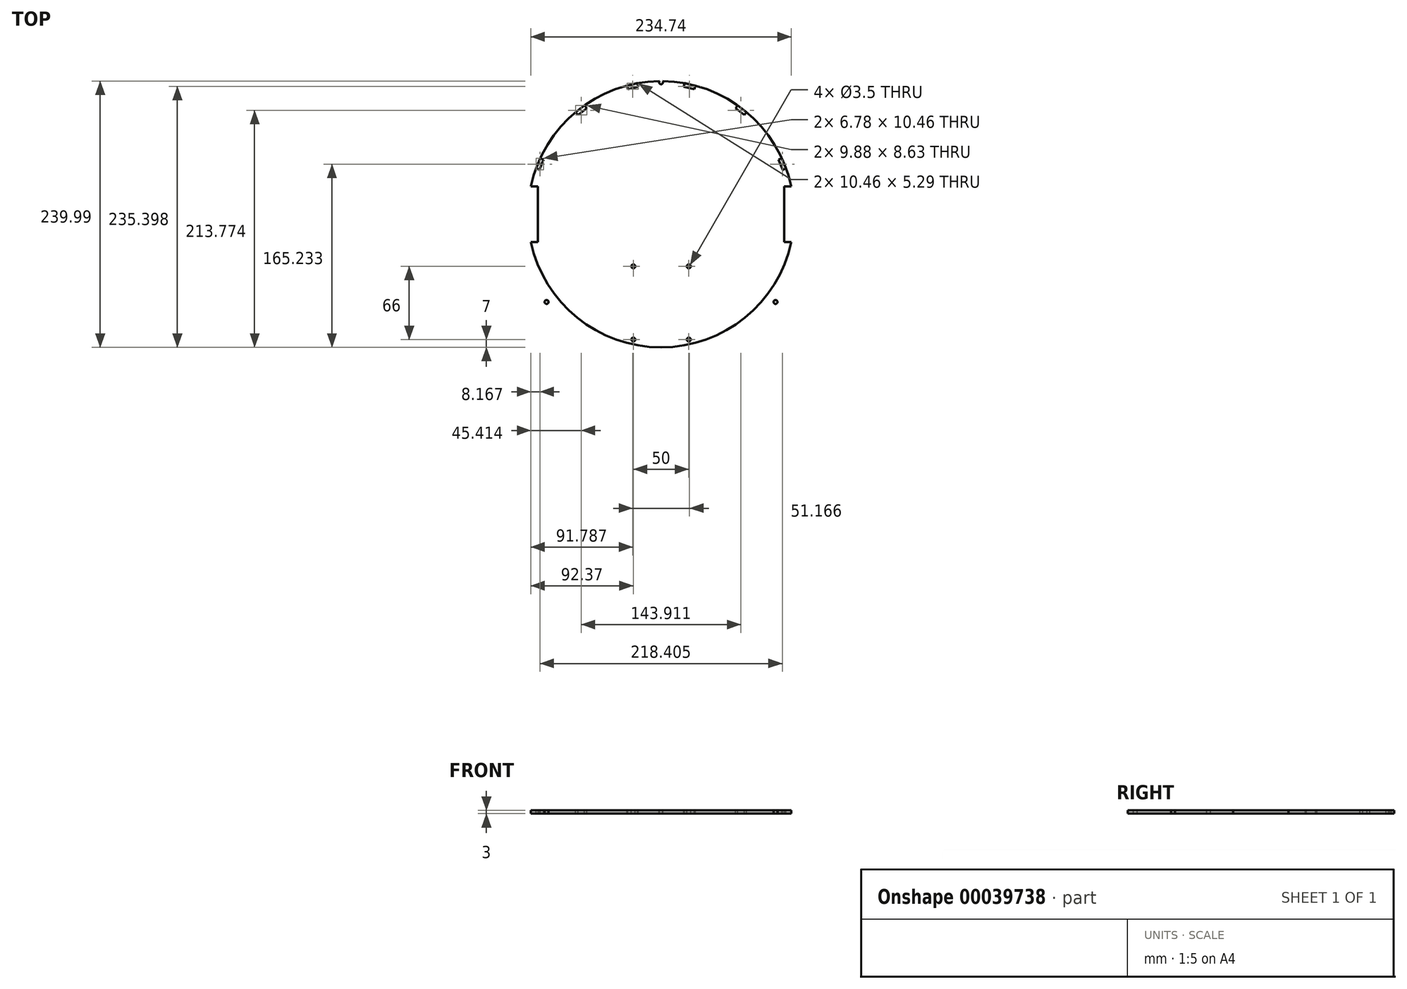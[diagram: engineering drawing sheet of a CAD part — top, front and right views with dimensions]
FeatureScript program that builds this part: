
annotation { "Feature Type Name" : "Feature", "Feature Type Description" : "" }
export const myFeature = defineFeature(function(context is Context, id is Id, definition is map)
    precondition{}
    {
        {
            var Q0;
            Q0=qCreatedBy(makeId("Top.planeOp"),FACE);
            var sketch = newSketch(context, id + "F0", { "sketchPlane" : qUnion([Q0])});
            skCircle(sketch, "E0", {"center": v(0, 0) * mm, "radius": 150 * mm});
            skLineSegment(sketch, "E1.bottom", {"start": v(-125, 25) * mm, "end": v(-111, 25) * mm});
            skLineSegment(sketch, "E1.top", {"start": v(-125, -25) * mm, "end": v(-111, -25) * mm});
            skLineSegment(sketch, "E1.left", {"start": v(-125, 25) * mm, "end": v(-125, -25) * mm});
            skLineSegment(sketch, "E1.right", {"start": v(-111, 25) * mm, "end": v(-111, -25) * mm});
            skLineSegment(sketch, "E2.bottom", {"start": v(125, 25) * mm, "end": v(111, 25) * mm});
            skLineSegment(sketch, "E2.top", {"start": v(125, -25) * mm, "end": v(111, -25) * mm});
            skLineSegment(sketch, "E2.left", {"start": v(125, 25) * mm, "end": v(125, -25) * mm});
            skLineSegment(sketch, "E2.right", {"start": v(111, 25) * mm, "end": v(111, -25) * mm});
            skCircle(sketch, "E3", {"center": v(-138, 19) * mm, "radius": 1.75 * mm});
            skCircle(sketch, "E4", {"center": v(-138, -19) * mm, "radius": 1.75 * mm});
            skCircle(sketch, "E5", {"center": v(138, 19) * mm, "radius": 1.75 * mm});
            skCircle(sketch, "E6", {"center": v(138, -19) * mm, "radius": 1.75 * mm});
            skSolve(sketch);
        }
        {
            var Q0;
            Q0=makeQuery(id+"F0.imprint","IMPRINT",FACE,{"disambiguationData":[TD([[makeQuery(id+"F0.imprint","IMPRINT",EDGE,{"derivedFrom":sQuery(id+"F0.wireOp",EDGE,"E0")}),1.0]])]});
            extrude(context, id + "F1", {"entities" : qUnion([Q0]), "depth" : 3 * mm});
        }
        {
            var Q0;
            Q0=makeQuery(id+"F1.opExtrude","CAP_FACE",FACE,{"disambiguationData":[OSD([sQuery(id+"F0.wireOp",EDGE,"E0"),sQuery(id+"F0.wireOp",EDGE,"E1.bottom"),sQuery(id+"F0.wireOp",EDGE,"E1.top"),sQuery(id+"F0.wireOp",EDGE,"E1.left"),sQuery(id+"F0.wireOp",EDGE,"E1.right"),sQuery(id+"F0.wireOp",EDGE,"E2.bottom"),sQuery(id+"F0.wireOp",EDGE,"E2.top"),sQuery(id+"F0.wireOp",EDGE,"E2.left"),sQuery(id+"F0.wireOp",EDGE,"E2.right")])],"isStart":false});
            var sketch = newSketch(context, id + "F2", { "sketchPlane" : qUnion([Q0])});
            skCircle(sketch, "E7", {"center": v(0, 0) * mm, "radius": 130 * mm, "construction": true});
            skLineSegment(sketch, "E8", {"start": v(0, 0) * mm, "end": v(0, 150) * mm, "construction": true});
            skLineSegment(sketch, "E9", {"start": v(0, 0) * mm, "end": v(-63.4, 135.95) * mm, "construction": true});
            skLineSegment(sketch, "E10", {"start": v(0, 0) * mm, "end": v(63.4, 135.95) * mm, "construction": true});
            skLineSegment(sketch, "E11", {"start": v(0, 0) * mm, "end": v(-147.72, 26.05) * mm, "construction": true});
            skLineSegment(sketch, "E12", {"start": v(0, 0) * mm, "end": v(147.72, 26.05) * mm, "construction": true});
            skCircle(sketch, "E13", {"center": v(-123.26, 41.31) * mm, "radius": 1.75 * mm});
            skCircle(sketch, "E14", {"center": v(-116.37, 57.94) * mm, "radius": 1.75 * mm});
            skCircle(sketch, "E15", {"center": v(-86.09, 97.4) * mm, "radius": 1.75 * mm});
            skCircle(sketch, "E16", {"center": v(-71.8, 108.37) * mm, "radius": 1.75 * mm});
            skCircle(sketch, "E17", {"center": v(-36.86, 124.67) * mm, "radius": 1.75 * mm});
            skCircle(sketch, "E18", {"center": v(-19.28, 128.56) * mm, "radius": 1.75 * mm});
            skCircle(sketch, "E19", {"center": v(19.28, 128.56) * mm, "radius": 1.75 * mm});
            skCircle(sketch, "E20", {"center": v(36.86, 124.67) * mm, "radius": 1.75 * mm});
            skCircle(sketch, "E21", {"center": v(71.8, 108.37) * mm, "radius": 1.75 * mm});
            skCircle(sketch, "E22", {"center": v(86.09, 97.4) * mm, "radius": 1.75 * mm});
            skCircle(sketch, "E23", {"center": v(116.37, 57.94) * mm, "radius": 1.75 * mm});
            skCircle(sketch, "E24", {"center": v(123.26, 41.31) * mm, "radius": 1.75 * mm});
            skLineSegment(sketch, "E25", {"start": v(0, 0) * mm, "end": v(-138.58, 57.4) * mm, "construction": true});
            skLineSegment(sketch, "E26", {"start": v(0, 0) * mm, "end": v(-91.31, 119) * mm, "construction": true});
            skLineSegment(sketch, "E27", {"start": v(0, 0) * mm, "end": v(-32.47, 146.44) * mm, "construction": true});
            skLineSegment(sketch, "E28", {"start": v(0, 0) * mm, "end": v(32.47, 146.44) * mm, "construction": true});
            skLineSegment(sketch, "E29", {"start": v(0, 0) * mm, "end": v(91.31, 119) * mm, "construction": true});
            skLineSegment(sketch, "E30", {"start": v(0, 0) * mm, "end": v(138.58, 57.4) * mm, "construction": true});
            skLineSegment(sketch, "E31", {"start": v(-130.33, 48.57) * mm, "end": v(-126.5, 57.81) * mm});
            skLineSegment(sketch, "E32", {"start": v(-126.5, 57.81) * mm, "end": v(-123.55, 56.59) * mm});
            skLineSegment(sketch, "E33", {"start": v(-123.55, 56.59) * mm, "end": v(-127.38, 47.35) * mm});
            skLineSegment(sketch, "E34", {"start": v(-127.38, 47.35) * mm, "end": v(-130.33, 48.57) * mm});
            skPoint(sketch, "E35", {"position": v(-128.42, 53.2) * mm});
            skLineSegment(sketch, "E36", {"start": v(-108.77, 50.46) * mm, "end": v(-112.6, 41.23) * mm});
            skLineSegment(sketch, "E37", {"start": v(-112.6, 41.23) * mm, "end": v(-109.64, 40) * mm});
            skLineSegment(sketch, "E38", {"start": v(-109.64, 40) * mm, "end": v(-105.81, 49.24) * mm});
            skLineSegment(sketch, "E39", {"start": v(-105.81, 49.24) * mm, "end": v(-108.77, 50.46) * mm});
            skPoint(sketch, "E40", {"position": v(-110.68, 45.85) * mm});
            skCircle(sketch, "E41", {"center": v(-118.07, 48.9) * mm, "radius": 1.75 * mm});
            skLineSegment(sketch, "E42.1.0", {"start": v(-78.7, 110.78) * mm, "end": v(-86.64, 104.7) * mm});
            skLineSegment(sketch, "E42.1.1", {"start": v(-88.58, 107.23) * mm, "end": v(-80.65, 113.32) * mm});
            skPoint(sketch, "E42.1.2", {"position": v(-84.62, 110.28) * mm});
            skLineSegment(sketch, "E42.1.3", {"start": v(-80.65, 113.32) * mm, "end": v(-78.7, 110.78) * mm});
            skLineSegment(sketch, "E42.1.4", {"start": v(-86.64, 104.7) * mm, "end": v(-88.58, 107.23) * mm});
            skPoint(sketch, "E42.1.5", {"position": v(-84.62, 110.28) * mm});
            skCircle(sketch, "E42.1.6", {"center": v(-77.8, 101.4) * mm, "radius": 1.75 * mm});
            skLineSegment(sketch, "E42.1.7", {"start": v(-68.96, 98.09) * mm, "end": v(-76.9, 92) * mm});
            skLineSegment(sketch, "E42.1.8", {"start": v(-74.95, 89.46) * mm, "end": v(-67.01, 95.55) * mm});
            skLineSegment(sketch, "E42.1.9", {"start": v(-67.01, 95.55) * mm, "end": v(-68.96, 98.09) * mm});
            skPoint(sketch, "E42.1.10", {"position": v(-72.93, 95.04) * mm});
            skLineSegment(sketch, "E42.1.11", {"start": v(-76.9, 92) * mm, "end": v(-74.95, 89.46) * mm});
            skLineSegment(sketch, "E42.anchor1", {"start": v(0, 0) * mm, "end": v(-118.07, 48.9) * mm, "construction": true});
            skLineSegment(sketch, "E42.anchor2", {"start": v(0, 0) * mm, "end": v(-77.8, 101.4) * mm, "construction": true});
            skLineSegment(sketch, "E43.1.0", {"start": v(78.7, 110.78) * mm, "end": v(80.65, 113.32) * mm});
            skLineSegment(sketch, "E43.1.1", {"start": v(86.64, 104.7) * mm, "end": v(78.7, 110.78) * mm});
            skLineSegment(sketch, "E43.1.2", {"start": v(88.58, 107.23) * mm, "end": v(86.64, 104.7) * mm});
            skCircle(sketch, "E43.1.3", {"center": v(77.8, 101.4) * mm, "radius": 1.75 * mm});
            skLineSegment(sketch, "E43.1.4", {"start": v(80.65, 113.32) * mm, "end": v(88.58, 107.23) * mm});
            skPoint(sketch, "E43.1.5", {"position": v(84.62, 110.28) * mm});
            skPoint(sketch, "E43.1.6", {"position": v(84.62, 110.28) * mm});
            skLineSegment(sketch, "E43.1.7", {"start": v(74.95, 89.46) * mm, "end": v(76.9, 92) * mm});
            skLineSegment(sketch, "E43.1.8", {"start": v(67.01, 95.55) * mm, "end": v(74.95, 89.46) * mm});
            skPoint(sketch, "E43.1.9", {"position": v(72.93, 95.04) * mm});
            skLineSegment(sketch, "E43.1.10", {"start": v(68.96, 98.09) * mm, "end": v(67.01, 95.55) * mm});
            skLineSegment(sketch, "E43.1.11", {"start": v(76.9, 92) * mm, "end": v(68.96, 98.09) * mm});
            skLineSegment(sketch, "E43.1.12", {"start": v(127.38, 47.35) * mm, "end": v(123.55, 56.59) * mm});
            skLineSegment(sketch, "E43.1.13", {"start": v(126.5, 57.81) * mm, "end": v(130.33, 48.57) * mm});
            skLineSegment(sketch, "E43.1.14", {"start": v(123.55, 56.59) * mm, "end": v(126.5, 57.81) * mm});
            skLineSegment(sketch, "E43.1.15", {"start": v(130.33, 48.57) * mm, "end": v(127.38, 47.35) * mm});
            skCircle(sketch, "E43.1.16", {"center": v(118.07, 48.9) * mm, "radius": 1.75 * mm});
            skPoint(sketch, "E43.1.17", {"position": v(128.42, 53.2) * mm});
            skPoint(sketch, "E43.1.18", {"position": v(128.42, 53.2) * mm});
            skLineSegment(sketch, "E43.1.19", {"start": v(109.64, 40) * mm, "end": v(112.6, 41.23) * mm});
            skLineSegment(sketch, "E43.1.20", {"start": v(105.81, 49.24) * mm, "end": v(109.64, 40) * mm});
            skPoint(sketch, "E43.1.21", {"position": v(110.68, 45.85) * mm});
            skLineSegment(sketch, "E43.1.22", {"start": v(108.77, 50.46) * mm, "end": v(105.81, 49.24) * mm});
            skLineSegment(sketch, "E43.1.23", {"start": v(112.6, 41.23) * mm, "end": v(108.77, 50.46) * mm});
            skLineSegment(sketch, "E43.anchor2", {"start": v(0, 0) * mm, "end": v(77.8, 101.4) * mm, "construction": true});
            skLineSegment(sketch, "E44.1.0", {"start": v(-34.97, 134.62) * mm, "end": v(-25.2, 136.79) * mm});
            skPoint(sketch, "E44.1.1", {"position": v(-30.09, 135.7) * mm});
            skLineSegment(sketch, "E44.1.2", {"start": v(-34.27, 131.5) * mm, "end": v(-34.97, 134.62) * mm});
            skCircle(sketch, "E44.1.3", {"center": v(-27.66, 124.77) * mm, "radius": 1.75 * mm});
            skLineSegment(sketch, "E44.1.4", {"start": v(-25.2, 136.79) * mm, "end": v(-24.51, 133.66) * mm});
            skLineSegment(sketch, "E44.1.5", {"start": v(-24.51, 133.66) * mm, "end": v(-34.27, 131.5) * mm});
            skPoint(sketch, "E44.1.6", {"position": v(-25.93, 116.96) * mm});
            skPoint(sketch, "E44.1.7", {"position": v(-30.09, 135.7) * mm});
            skLineSegment(sketch, "E44.1.8", {"start": v(-30.81, 115.88) * mm, "end": v(-30.12, 112.75) * mm});
            skLineSegment(sketch, "E44.1.9", {"start": v(-20.36, 114.92) * mm, "end": v(-21.05, 118.04) * mm});
            skLineSegment(sketch, "E44.1.10", {"start": v(-30.12, 112.75) * mm, "end": v(-20.36, 114.92) * mm});
            skLineSegment(sketch, "E44.1.11", {"start": v(-21.05, 118.04) * mm, "end": v(-30.81, 115.88) * mm});
            skLineSegment(sketch, "E44.anchor2", {"start": v(0, 0) * mm, "end": v(-27.66, 124.77) * mm, "construction": true});
            skLineSegment(sketch, "E45.1.0", {"start": v(25.2, 136.79) * mm, "end": v(34.97, 134.62) * mm});
            skLineSegment(sketch, "E45.1.1", {"start": v(24.51, 133.66) * mm, "end": v(25.2, 136.79) * mm});
            skLineSegment(sketch, "E45.1.2", {"start": v(34.27, 131.5) * mm, "end": v(24.51, 133.66) * mm});
            skLineSegment(sketch, "E45.1.3", {"start": v(34.97, 134.62) * mm, "end": v(34.27, 131.5) * mm});
            skPoint(sketch, "E45.1.4", {"position": v(30.09, 135.7) * mm});
            skPoint(sketch, "E45.1.5", {"position": v(30.09, 135.7) * mm});
            skCircle(sketch, "E45.1.6", {"center": v(27.66, 124.77) * mm, "radius": 1.75 * mm});
            skLineSegment(sketch, "E45.1.7", {"start": v(30.81, 115.88) * mm, "end": v(21.05, 118.04) * mm});
            skLineSegment(sketch, "E45.1.8", {"start": v(30.12, 112.75) * mm, "end": v(30.81, 115.88) * mm});
            skPoint(sketch, "E45.1.9", {"position": v(25.93, 116.96) * mm});
            skLineSegment(sketch, "E45.1.10", {"start": v(20.36, 114.92) * mm, "end": v(30.12, 112.75) * mm});
            skLineSegment(sketch, "E45.1.11", {"start": v(21.05, 118.04) * mm, "end": v(20.36, 114.92) * mm});
            skLineSegment(sketch, "E45.anchor2", {"start": v(0, 0) * mm, "end": v(27.66, 124.77) * mm, "construction": true});
            skSolve(sketch);
        }
        {
            var Q0;
            Q0 = qSketchRegion(id + "F2", true);
            var Q1;
            Q1=makeQuery(id+"F1.opExtrude","CAP_FACE",FACE,{"disambiguationData":[OSD([sQuery(id+"F0.wireOp",EDGE,"E0"),sQuery(id+"F0.wireOp",EDGE,"E1.bottom"),sQuery(id+"F0.wireOp",EDGE,"E1.top"),sQuery(id+"F0.wireOp",EDGE,"E1.left"),sQuery(id+"F0.wireOp",EDGE,"E1.right"),sQuery(id+"F0.wireOp",EDGE,"E2.bottom"),sQuery(id+"F0.wireOp",EDGE,"E2.top"),sQuery(id+"F0.wireOp",EDGE,"E2.left"),sQuery(id+"F0.wireOp",EDGE,"E2.right")])],"isStart":true});
            extrude(context, id + "F3", {"entities" : qUnion([Q0]), "operationType" : NewBodyOperationType.REMOVE, "endBound" : BoundingType.UP_TO_SURFACE, "oppositeDirection" : true, "endBoundEntityFace" : qUnion([Q1]), "depth" : 25 * mm});
        }
        {
            var Q0;
            Q0=makeQuery(id+"F1.opExtrude","CAP_FACE",FACE,{"disambiguationData":[OSD([sQuery(id+"F0.wireOp",EDGE,"E0"),sQuery(id+"F0.wireOp",EDGE,"E1.bottom"),sQuery(id+"F0.wireOp",EDGE,"E1.top"),sQuery(id+"F0.wireOp",EDGE,"E1.left"),sQuery(id+"F0.wireOp",EDGE,"E1.right"),sQuery(id+"F0.wireOp",EDGE,"E2.bottom"),sQuery(id+"F0.wireOp",EDGE,"E2.top"),sQuery(id+"F0.wireOp",EDGE,"E2.left"),sQuery(id+"F0.wireOp",EDGE,"E2.right"),sQuery(id+"F0.wireOp",EDGE,"E3"),sQuery(id+"F0.wireOp",EDGE,"E4"),sQuery(id+"F0.wireOp",EDGE,"E5"),sQuery(id+"F0.wireOp",EDGE,"E6")])],"isStart":false});
            var sketch = newSketch(context, id + "F4", { "sketchPlane" : qUnion([Q0])});
            skCircle(sketch, "E46", {"center": v(0, 135) * mm, "radius": 10 * mm});
            skLineSegment(sketch, "E47.bottom", {"start": v(-15, 150) * mm, "end": v(15, 150) * mm, "construction": true});
            skLineSegment(sketch, "E47.top", {"start": v(-15, 120) * mm, "end": v(15, 120) * mm, "construction": true});
            skLineSegment(sketch, "E47.left", {"start": v(-15, 150) * mm, "end": v(-15, 120) * mm, "construction": true});
            skLineSegment(sketch, "E47.right", {"start": v(15, 150) * mm, "end": v(15, 120) * mm, "construction": true});
            skCircle(sketch, "E48", {"center": v(15, 142) * mm, "radius": 1.75 * mm});
            skCircle(sketch, "E49", {"center": v(0, 119) * mm, "radius": 1.75 * mm});
            skCircle(sketch, "E50", {"center": v(-15, 142) * mm, "radius": 1.75 * mm});
            skLineSegment(sketch, "E51", {"start": v(-15, 142) * mm, "end": v(15, 142) * mm, "construction": true});
            skLineSegment(sketch, "E52", {"start": v(15, 142) * mm, "end": v(0, 119) * mm, "construction": true});
            skLineSegment(sketch, "E53", {"start": v(0, 119) * mm, "end": v(-15, 142) * mm, "construction": true});
            skSolve(sketch);
        }
        {
            var Q0;
            Q0=makeQuery(id+"F4.imprint","IMPRINT",FACE,{"disambiguationData":[TD([[makeQuery(id+"F4.imprint","IMPRINT",EDGE,{"derivedFrom":sQuery(id+"F4.wireOp",EDGE,"E50")}),1.0]])]});
            var Q1;
            Q1=makeQuery(id+"F4.imprint","IMPRINT",FACE,{"disambiguationData":[TD([[makeQuery(id+"F4.imprint","IMPRINT",EDGE,{"derivedFrom":sQuery(id+"F4.wireOp",EDGE,"E48")}),1.0]])]});
            var Q2;
            Q2=makeQuery(id+"F4.imprint","IMPRINT",FACE,{"disambiguationData":[TD([[makeQuery(id+"F4.imprint","IMPRINT",EDGE,{"derivedFrom":sQuery(id+"F4.wireOp",EDGE,"E49")}),1.0]])]});
            var Q3;
            Q3=makeQuery(id+"F4.imprint","IMPRINT",FACE,{"disambiguationData":[TD([[makeQuery(id+"F4.imprint","IMPRINT",EDGE,{"derivedFrom":sQuery(id+"F4.wireOp",EDGE,"E46")}),1.0]])]});
            var Q4;
            Q4=makeQuery(id+"F4.imprint","IMPRINT",FACE,{"disambiguationData":[TD([[makeQuery(id+"F4.imprint","IMPRINT",EDGE,{"derivedFrom":sQuery(id+"F4.wireOp",EDGE,"2579ac32-ccdb-4afd-8fe6-3aab5110a1ee")}),1.0]])]});
            var Q5;
            Q5=sQuery(id+"F4.wireOp",EDGE,"E47.left");
            extrude(context, id + "F5", {"entities" : qUnion([Q0, Q1, Q2, Q3, Q4]), "operationType" : NewBodyOperationType.REMOVE, "surfaceEntities" : qUnion([Q5]), "endBound" : BoundingType.UP_TO_NEXT, "oppositeDirection" : true, "depth" : 25 * mm});
        }
        {
            var Q0;
            Q0=makeQuery(id+"F1.opExtrude","CAP_FACE",FACE,{"disambiguationData":[OSD([sQuery(id+"F0.wireOp",EDGE,"E0"),sQuery(id+"F0.wireOp",EDGE,"E1.bottom"),sQuery(id+"F0.wireOp",EDGE,"E1.top"),sQuery(id+"F0.wireOp",EDGE,"E1.left"),sQuery(id+"F0.wireOp",EDGE,"E1.right"),sQuery(id+"F0.wireOp",EDGE,"E2.bottom"),sQuery(id+"F0.wireOp",EDGE,"E2.top"),sQuery(id+"F0.wireOp",EDGE,"E2.left"),sQuery(id+"F0.wireOp",EDGE,"E2.right"),sQuery(id+"F0.wireOp",EDGE,"E3"),sQuery(id+"F0.wireOp",EDGE,"E4"),sQuery(id+"F0.wireOp",EDGE,"E5"),sQuery(id+"F0.wireOp",EDGE,"E6")])],"isStart":false});
            var sketch = newSketch(context, id + "F6", { "sketchPlane" : qUnion([Q0])});
            skCircle(sketch, "E54", {"center": v(0, 0) * mm, "radius": 150 * mm});
            skCircle(sketch, "E55.0", {"center": v(0, 0) * mm, "radius": 120 * mm});
            skLineSegment(sketch, "E56", {"start": v(0, 150) * mm, "end": v(0, -150) * mm, "construction": true});
            skLineSegment(sketch, "E57", {"start": v(150, 0) * mm, "end": v(-150, 0) * mm, "construction": true});
            skLineSegment(sketch, "E58", {"start": v(0, 0) * mm, "end": v(63.4, 135.95) * mm, "construction": true});
            skLineSegment(sketch, "E59", {"start": v(0, 0) * mm, "end": v(-63.4, 135.95) * mm, "construction": true});
            skLineSegment(sketch, "E60", {"start": v(0, 0) * mm, "end": v(-147.72, 26.05) * mm, "construction": true});
            skLineSegment(sketch, "E61", {"start": v(0, 0) * mm, "end": v(147.72, 26.05) * mm, "construction": true});
            skLineSegment(sketch, "E62", {"start": v(0, 0) * mm, "end": v(-119, 91.31) * mm, "construction": true});
            skCircle(sketch, "E63", {"center": v(-103.14, 79.14) * mm, "radius": 1.75 * mm});
            skLineSegment(sketch, "E64", {"start": v(-113.92, 73.3) * mm, "end": v(-105.99, 67.2) * mm});
            skLineSegment(sketch, "E65", {"start": v(-105.99, 67.2) * mm, "end": v(-104.04, 69.75) * mm});
            skLineSegment(sketch, "E66", {"start": v(-104.04, 69.75) * mm, "end": v(-111.97, 75.84) * mm});
            skLineSegment(sketch, "E67", {"start": v(-111.97, 75.84) * mm, "end": v(-113.92, 73.3) * mm});
            skPoint(sketch, "E68", {"position": v(-108, 72.8) * mm});
            skLineSegment(sketch, "E69.MirrorCS", {"start": v(-100.28, 91.07) * mm, "end": v(-92.35, 84.98) * mm});
            skLineSegment(sketch, "E70.MirrorCS", {"start": v(-94.3, 82.44) * mm, "end": v(-102.23, 88.53) * mm});
            skLineSegment(sketch, "E71.MirrorCS", {"start": v(-92.35, 84.98) * mm, "end": v(-94.3, 82.44) * mm});
            skLineSegment(sketch, "E72.MirrorCS", {"start": v(-102.23, 88.53) * mm, "end": v(-100.28, 91.07) * mm});
            skPoint(sketch, "E73", {"position": v(-95.2, 73.05) * mm});
            skLineSegment(sketch, "E74", {"start": v(-103.14, 79.14) * mm, "end": v(-108, 72.8) * mm, "construction": true});
            skLineSegment(sketch, "E75.1.0", {"start": v(103.14, 79.14) * mm, "end": v(98.27, 85.49) * mm, "construction": true});
            skLineSegment(sketch, "E75.1.1", {"start": v(102.23, 88.53) * mm, "end": v(100.28, 91.07) * mm});
            skLineSegment(sketch, "E75.1.2", {"start": v(94.3, 82.44) * mm, "end": v(102.23, 88.53) * mm});
            skLineSegment(sketch, "E75.1.3", {"start": v(92.35, 84.98) * mm, "end": v(94.3, 82.44) * mm});
            skLineSegment(sketch, "E75.1.4", {"start": v(100.28, 91.07) * mm, "end": v(92.35, 84.98) * mm});
            skCircle(sketch, "E75.1.5", {"center": v(103.14, 79.14) * mm, "radius": 1.75 * mm});
            skLineSegment(sketch, "E75.1.6", {"start": v(104.04, 69.75) * mm, "end": v(111.97, 75.84) * mm});
            skLineSegment(sketch, "E75.1.7", {"start": v(105.99, 67.2) * mm, "end": v(104.04, 69.75) * mm});
            skLineSegment(sketch, "E75.1.8", {"start": v(113.92, 73.3) * mm, "end": v(105.99, 67.2) * mm});
            skLineSegment(sketch, "E75.1.9", {"start": v(111.97, 75.84) * mm, "end": v(113.92, 73.3) * mm});
            skLineSegment(sketch, "E75.anchor1", {"start": v(0, 0) * mm, "end": v(-103.14, 79.14) * mm, "construction": true});
            skLineSegment(sketch, "E75.anchor2", {"start": v(0, 0) * mm, "end": v(103.14, 79.14) * mm, "construction": true});
            skLineSegment(sketch, "E76.MirrorCS", {"start": v(-113.92, -73.3) * mm, "end": v(-105.99, -67.2) * mm});
            skLineSegment(sketch, "E77.MirrorCS", {"start": v(-111.97, -75.84) * mm, "end": v(-113.92, -73.3) * mm});
            skLineSegment(sketch, "E78.MirrorCS", {"start": v(-104.04, -69.75) * mm, "end": v(-111.97, -75.84) * mm});
            skLineSegment(sketch, "E79.MirrorCS", {"start": v(-105.99, -67.2) * mm, "end": v(-104.04, -69.75) * mm});
            skCircle(sketch, "E80.MirrorC", {"center": v(-103.14, -79.14) * mm, "radius": 1.75 * mm});
            skLineSegment(sketch, "E81.MirrorCS", {"start": v(-94.3, -82.44) * mm, "end": v(-102.23, -88.53) * mm});
            skLineSegment(sketch, "E82.MirrorCS", {"start": v(-92.35, -84.98) * mm, "end": v(-94.3, -82.44) * mm});
            skLineSegment(sketch, "E83.MirrorCS", {"start": v(-100.28, -91.07) * mm, "end": v(-92.35, -84.98) * mm});
            skLineSegment(sketch, "E84.MirrorCS", {"start": v(-102.23, -88.53) * mm, "end": v(-100.28, -91.07) * mm});
            skLineSegment(sketch, "E85.MirrorCS", {"start": v(100.28, -91.07) * mm, "end": v(92.35, -84.98) * mm});
            skLineSegment(sketch, "E86.MirrorCS", {"start": v(102.23, -88.53) * mm, "end": v(100.28, -91.07) * mm});
            skLineSegment(sketch, "E87.MirrorCS", {"start": v(94.3, -82.44) * mm, "end": v(102.23, -88.53) * mm});
            skLineSegment(sketch, "E88.MirrorCS", {"start": v(92.35, -84.98) * mm, "end": v(94.3, -82.44) * mm});
            skCircle(sketch, "E89.MirrorC", {"center": v(103.14, -79.14) * mm, "radius": 1.75 * mm});
            skLineSegment(sketch, "E90.MirrorCS", {"start": v(104.04, -69.75) * mm, "end": v(111.97, -75.84) * mm});
            skLineSegment(sketch, "E91.MirrorCS", {"start": v(111.97, -75.84) * mm, "end": v(113.92, -73.3) * mm});
            skLineSegment(sketch, "E92.MirrorCS", {"start": v(113.92, -73.3) * mm, "end": v(105.99, -67.2) * mm});
            skLineSegment(sketch, "E93.MirrorCS", {"start": v(105.99, -67.2) * mm, "end": v(104.04, -69.75) * mm});
            skSolve(sketch);
        }
        {
            var Q0;
            Q0=makeQuery(id+"F6.imprint","IMPRINT",FACE,{"disambiguationData":[TD([[makeQuery(id+"F6.imprint","IMPRINT",EDGE,{"derivedFrom":sQuery(id+"F6.wireOp",EDGE,"E76.MirrorCS")}),-1.0]])]});
            var Q1;
            Q1=makeQuery(id+"F6.imprint","IMPRINT",FACE,{"disambiguationData":[TD([[makeQuery(id+"F6.imprint","IMPRINT",EDGE,{"derivedFrom":sQuery(id+"F6.wireOp",EDGE,"E80.MirrorC")}),-1.0]])]});
            var Q2;
            Q2=makeQuery(id+"F6.imprint","IMPRINT",FACE,{"disambiguationData":[TD([[makeQuery(id+"F6.imprint","IMPRINT",EDGE,{"derivedFrom":sQuery(id+"F6.wireOp",EDGE,"E81.MirrorCS")}),1.0]])]});
            var Q3;
            Q3=makeQuery(id+"F6.imprint","IMPRINT",FACE,{"disambiguationData":[TD([[makeQuery(id+"F6.imprint","IMPRINT",EDGE,{"derivedFrom":sQuery(id+"F6.wireOp",EDGE,"E85.MirrorCS")}),-1.0]])]});
            var Q4;
            Q4=makeQuery(id+"F6.imprint","IMPRINT",FACE,{"disambiguationData":[TD([[makeQuery(id+"F6.imprint","IMPRINT",EDGE,{"derivedFrom":sQuery(id+"F6.wireOp",EDGE,"E89.MirrorC")}),-1.0]])]});
            var Q5;
            Q5=makeQuery(id+"F6.imprint","IMPRINT",FACE,{"disambiguationData":[TD([[makeQuery(id+"F6.imprint","IMPRINT",EDGE,{"derivedFrom":sQuery(id+"F6.wireOp",EDGE,"E90.MirrorCS")}),1.0]])]});
            var Q6;
            Q6=makeQuery(id+"F6.imprint","IMPRINT",FACE,{"disambiguationData":[TD([[makeQuery(id+"F6.imprint","IMPRINT",EDGE,{"derivedFrom":sQuery(id+"F6.wireOp",EDGE,"E75.1.6")}),-1.0]])]});
            var Q7;
            Q7=makeQuery(id+"F6.imprint","IMPRINT",FACE,{"disambiguationData":[TD([[makeQuery(id+"F6.imprint","IMPRINT",EDGE,{"derivedFrom":sQuery(id+"F6.wireOp",EDGE,"E75.1.5")}),1.0]])]});
            var Q8;
            Q8=makeQuery(id+"F6.imprint","IMPRINT",FACE,{"disambiguationData":[TD([[makeQuery(id+"F6.imprint","IMPRINT",EDGE,{"derivedFrom":sQuery(id+"F6.wireOp",EDGE,"E75.1.1")}),1.0]])]});
            var Q9;
            Q9=makeQuery(id+"F6.imprint","IMPRINT",FACE,{"disambiguationData":[TD([[makeQuery(id+"F6.imprint","IMPRINT",EDGE,{"derivedFrom":sQuery(id+"F6.wireOp",EDGE,"E69.MirrorCS")}),-1.0]])]});
            var Q10;
            Q10=makeQuery(id+"F6.imprint","IMPRINT",FACE,{"disambiguationData":[TD([[makeQuery(id+"F6.imprint","IMPRINT",EDGE,{"derivedFrom":sQuery(id+"F6.wireOp",EDGE,"E63")}),1.0]])]});
            var Q11;
            Q11=makeQuery(id+"F6.imprint","IMPRINT",FACE,{"disambiguationData":[TD([[makeQuery(id+"F6.imprint","IMPRINT",EDGE,{"derivedFrom":sQuery(id+"F6.wireOp",EDGE,"E64")}),1.0]])]});
            extrude(context, id + "F7", {"entities" : qUnion([Q0, Q1, Q2, Q3, Q4, Q5, Q6, Q7, Q8, Q9, Q10, Q11]), "operationType" : NewBodyOperationType.REMOVE, "oppositeDirection" : true, "depth" : 25 * mm});
        }
        {
            var Q0;
            Q0=makeQuery(id+"F1.opExtrude","CAP_FACE",FACE,{"disambiguationData":[OSD([sQuery(id+"F0.wireOp",EDGE,"E0"),sQuery(id+"F0.wireOp",EDGE,"E1.bottom"),sQuery(id+"F0.wireOp",EDGE,"E1.top"),sQuery(id+"F0.wireOp",EDGE,"E1.left"),sQuery(id+"F0.wireOp",EDGE,"E1.right"),sQuery(id+"F0.wireOp",EDGE,"E2.bottom"),sQuery(id+"F0.wireOp",EDGE,"E2.top"),sQuery(id+"F0.wireOp",EDGE,"E2.left"),sQuery(id+"F0.wireOp",EDGE,"E2.right"),sQuery(id+"F0.wireOp",EDGE,"E3"),sQuery(id+"F0.wireOp",EDGE,"E4"),sQuery(id+"F0.wireOp",EDGE,"E5"),sQuery(id+"F0.wireOp",EDGE,"E6")])],"isStart":false});
            var sketch = newSketch(context, id + "F8", { "sketchPlane" : qUnion([Q0])});
            skLineSegment(sketch, "E94.rect.bottom", {"start": v(25, -47) * mm, "end": v(-25, -47) * mm, "construction": true});
            skLineSegment(sketch, "E94.rect.top", {"start": v(25, -113) * mm, "end": v(-25, -113) * mm, "construction": true});
            skLineSegment(sketch, "E94.rect.left", {"start": v(25, -47) * mm, "end": v(25, -113) * mm, "construction": true});
            skLineSegment(sketch, "E94.rect.right", {"start": v(-25, -47) * mm, "end": v(-25, -113) * mm, "construction": true});
            skPoint(sketch, "E94.rect.middle", {"position": v(0, -80) * mm});
            skLineSegment(sketch, "E95.rect.bottom", {"start": v(80, 32.5) * mm, "end": v(-80, 32.5) * mm, "construction": true});
            skLineSegment(sketch, "E95.rect.top", {"start": v(80, -32.5) * mm, "end": v(-80, -32.5) * mm, "construction": true});
            skLineSegment(sketch, "E95.rect.left", {"start": v(80, 32.5) * mm, "end": v(80, -32.5) * mm, "construction": true});
            skLineSegment(sketch, "E95.rect.right", {"start": v(-80, 32.5) * mm, "end": v(-80, -32.5) * mm, "construction": true});
            skPoint(sketch, "E95.rect.middle", {"position": v(0, 0) * mm});
            skSolve(sketch);
        }
        {
            var Q0;
            Q0=sQuery(id+"F8.wireOp",VERTEX,"E94.rect.right.start");
            var Q1;
            Q1=sQuery(id+"F8.wireOp",VERTEX,"E94.rect.left.start");
            var Q2;
            Q2=sQuery(id+"F8.wireOp",VERTEX,"E94.rect.left.end");
            var Q3;
            Q3=sQuery(id+"F8.wireOp",VERTEX,"E94.rect.right.end");
            var Q4;
            Q4=makeQuery(id+"F1.opExtrude","SWEPT_BODY",BODY,{"disambiguationData":[OSD([sQuery(id+"F0.wireOp",EDGE,"E0"),sQuery(id+"F0.wireOp",EDGE,"E1.bottom"),sQuery(id+"F0.wireOp",EDGE,"E1.top"),sQuery(id+"F0.wireOp",EDGE,"E1.left"),sQuery(id+"F0.wireOp",EDGE,"E1.right"),sQuery(id+"F0.wireOp",EDGE,"E2.bottom"),sQuery(id+"F0.wireOp",EDGE,"E2.top"),sQuery(id+"F0.wireOp",EDGE,"E2.left"),sQuery(id+"F0.wireOp",EDGE,"E2.right"),sQuery(id+"F0.wireOp",EDGE,"E3"),sQuery(id+"F0.wireOp",EDGE,"E4"),sQuery(id+"F0.wireOp",EDGE,"E5"),sQuery(id+"F0.wireOp",EDGE,"E6")])]});
            hole(context, id + "F9", {"style" : HoleStyle.SIMPLE, "holeDiameter" : 3.5 * mm, "endStyle" : HoleEndStyle.THROUGH, "locations" : qUnion([Q0, Q1, Q2, Q3]), "scope" : qUnion([Q4])});
        }
    });
